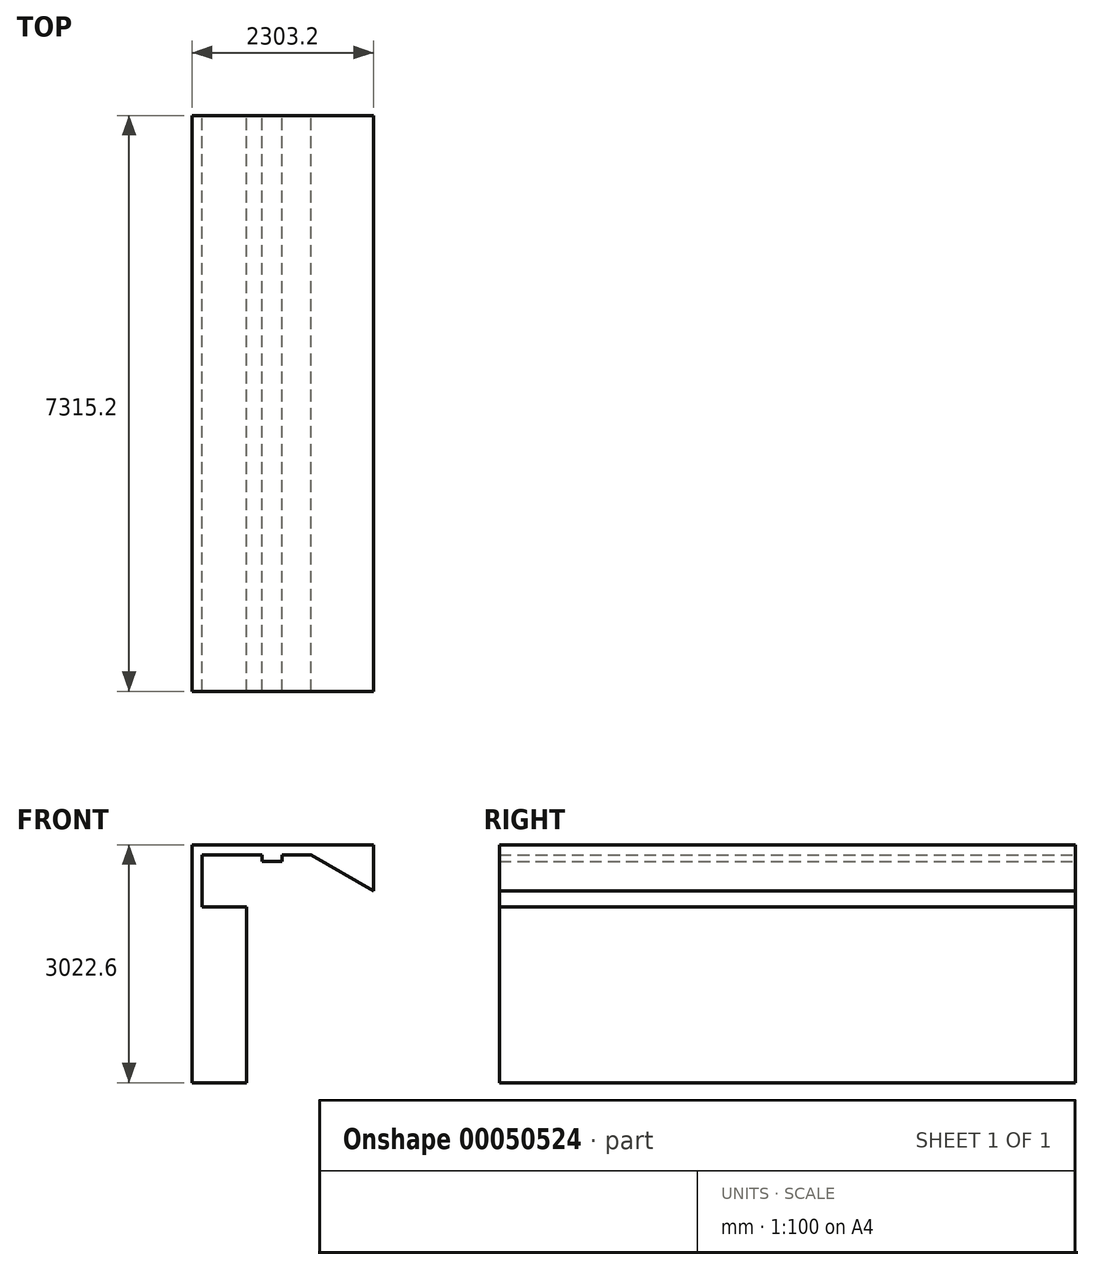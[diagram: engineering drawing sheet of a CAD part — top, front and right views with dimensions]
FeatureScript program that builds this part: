
annotation { "Feature Type Name" : "Feature", "Feature Type Description" : "" }
export const myFeature = defineFeature(function(context is Context, id is Id, definition is map)
    precondition{}
    {
        {
            var Q0;
            Q0=qCreatedBy(makeId("Front.planeOp"),FACE);
            var sketch = newSketch(context, id + "F0", { "sketchPlane" : qUnion([Q0])});
            skLineSegment(sketch, "E0", {"start": v(-459.45, 723.9) * mm, "end": v(-459.45, -1511.3) * mm});
            skLineSegment(sketch, "E1", {"start": v(-459.45, -1511.3) * mm, "end": v(-1151.6, -1511.3) * mm});
            skLineSegment(sketch, "E2", {"start": v(-1151.6, -1511.3) * mm, "end": v(-1151.6, 1511.3) * mm});
            skLineSegment(sketch, "E3", {"start": v(-1151.6, 1511.3) * mm, "end": v(1151.6, 1511.3) * mm});
            skLineSegment(sketch, "E4", {"start": v(1151.6, 1511.3) * mm, "end": v(1151.6, 927.1) * mm});
            skLineSegment(sketch, "E5", {"start": v(359.7, 1384.3) * mm, "end": v(1151.6, 927.1) * mm});
            skLineSegment(sketch, "E6", {"start": v(359.7, 1384.3) * mm, "end": v(-8.6, 1384.3) * mm});
            skLineSegment(sketch, "E7", {"start": v(-8.6, 1384.3) * mm, "end": v(-8.6, 1301.75) * mm});
            skLineSegment(sketch, "E8", {"start": v(-8.6, 1301.75) * mm, "end": v(-262.6, 1301.75) * mm});
            skLineSegment(sketch, "E9", {"start": v(-262.6, 1301.75) * mm, "end": v(-262.6, 1384.3) * mm});
            skLineSegment(sketch, "E10", {"start": v(-262.6, 1384.3) * mm, "end": v(-1024.6, 1384.3) * mm});
            skLineSegment(sketch, "E11", {"start": v(-1024.6, 1384.3) * mm, "end": v(-1024.6, 723.9) * mm});
            skLineSegment(sketch, "E12", {"start": v(-1024.6, 723.9) * mm, "end": v(-459.45, 723.9) * mm});
            skLineSegment(sketch, "E13", {"start": v(1151.6, 1511.3) * mm, "end": v(-1151.6, -1511.3) * mm, "construction": true});
            skSolve(sketch);
        }
        {
            var Q0;
            Q0 = qSketchRegion(id + "F0", true);
            extrude(context, id + "F1", {"entities" : qUnion([Q0]), "endBound" : BoundingType.SYMMETRIC, "depth" : 7315.2 * mm});
        }
    });
